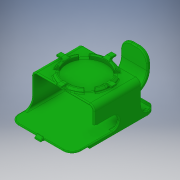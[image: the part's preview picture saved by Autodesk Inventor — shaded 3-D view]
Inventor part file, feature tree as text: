
AUTODESK INVENTOR PART (.ipt)
format: ipt  version: 2019.4 (Build 234330000, 330)  size: 2,206,208 bytes
history: native  units: in
note: dims shown in document units (in); Inventor stores cm internally (conversion verified against a paired STEP export)
features: sketch x43, extrude x41, fillet x30, other x8, reference x8, plane x7, projected_geometry x7, chamfer x5, pattern_circular x1
ambient origin geometry x8: Origin, YZ Plane, XZ Plane, XY Plane, X Axis, Y Axis, Z Axis, Center Point
bodies: Solid1 (feature_tree)
feature tree (150):
  plane  "Work Plane1"
  other  "BasePlate"
  extrude  "Extrusion1"  Depth=0.748in
  extrude  "Extrusion2"  Depth=0.748in
  sketch  "Sketch2"  dims[d0=0.5906in d3=0.748in]
  plane  "Work Plane2"
  extrude  "Extrusion3"  Depth=0.3937in TaperAngle=0.0deg
  extrude  "Extrusion4"  TaperAngle=0.0deg  [1 undecoded]
  extrude  "Extrusion5"  Depth=0.0394in TaperAngle=0.0deg
  extrude  "Extrusion6"  Depth=0.5906in TaperAngle=0.0deg
  plane  "Work Plane4"
  sketch  "Sketch6"  dims[d9=0.2559in d10=0.0in]
  plane  "Work Plane3"
  plane  "Work Plane6"
  extrude  "Extrusion9"  Depth=0.3937in
  fillet  "Fillet13"  Radius=0.5906in
  plane  "Work Plane7"
  extrude  "Extrusion10"  Depth=0.5906in
  sketch  "Sketch13"  dims[d15=3.937in d16=0.5906in d17=0.0in]
  extrude  "Extrusion12"  Depth=0.2362in TaperAngle=0.0deg
  extrude  "Extrusion13"  Depth=0.2362in TaperAngle=0.0deg
  extrude  "Extrusion14"  Depth=0.0787in TaperAngle=0.0deg
  extrude  "Extrusion15"  Depth=0.3543in TaperAngle=0.0deg
  extrude  "Extrusion16"  Depth=0.0394in TaperAngle=0.0deg
  extrude  "Extrusion17"  Depth=0.0787in TaperAngle=0.0deg
  extrude  "Extrusion18"  TaperAngle=0.0deg  [1 undecoded]
  extrude  "Extrusion19"  Depth=0.1969in TaperAngle=0.0deg
  sketch  "Sketch22"  dims[d85=0.1378in d86=0.0in]
  sketch  "Sketch23"  dims[d87=0.8519in d88=0.0in d89=0.1969in d90=0.0in]
  plane  "Work Plane8"
  extrude  "Extrusion20"  Depth=0.1378in
  extrude  "Extrusion21"  Depth=0.0787in
  extrude  "Extrusion22"  Depth=0.1181in TaperAngle=0.0deg
  extrude  "Extrusion23"  Depth=0.0394in
  extrude  "Extrusion24"  Depth=0.1181in TaperAngle=0.0deg
  extrude  "Extrusion25"  Depth=0.0394in
  chamfer  "Chamfer2"  Distance=2.3622in Angle=360.0deg
  extrude  "Extrusion26"  Depth=0.1181in TaperAngle=0.0deg
  chamfer  "Chamfer3"  Distance=0.1102in Angle=45.0deg
  extrude  "Extrusion27"  Depth=0.3937in
  extrude  "Extrusion28"  Depth=0.1181in TaperAngle=45.0deg
  fillet  "Fillet16"  Radius=0.0787in
  chamfer  "Chamfer4"  Distance=0.0787in
  fillet  "Fillet17"  Radius=0.0787in
  fillet  "Fillet18"  Radius=0.0787in
  fillet  "Fillet19"  Radius=0.0394in
  chamfer  "Chamfer5"  Distance=0.0394in
  extrude  "Extrusion29"  Depth=0.7874in
  extrude  "Extrusion30"  Depth=0.0394in TaperAngle=0.0deg
  extrude  "Extrusion31"  Depth=0.0394in TaperAngle=0.0deg
  extrude  "Extrusion32"  Depth=0.1575in
  extrude  "Extrusion33"  Depth=0.1181in TaperAngle=0.0deg
  extrude  "Extrusion34"  Depth=0.1289in TaperAngle=45.0deg
  fillet  "Fillet30"  Radius=0.5413in
  extrude  "Extrusion35"  Depth=1.9685in
  extrude  "Extrusion36"  Depth=2.3622in
  extrude  "Extrusion37"  Depth=0.0394in TaperAngle=0.0deg
  extrude  "Extrusion38"  Depth=0.0394in TaperAngle=0.0deg
  extrude  "Extrusion39"  Depth=0.4828in
  fillet  "Fillet31"  Radius=0.2953in
  chamfer  "Chamfer7"  Distance=0.063in
  fillet  "Fillet32"  Radius=0.063in
  sketch  "Sketch42"  dims[d181=1.9685in d182=2.3622in]
  sketch  "Sketch43"  dims[d183=2.3622in d184=0.0394in d185=0.0in]
  extrude  "Extrusion40"  Depth=0.063in
  sketch  "Sketch45"  dims[d209=0.1181in d210=0.0in d219=0.4828in d220=0.2953in]
  extrude  "Extrusion41"  Depth=0.0394in
  extrude  "Extrusion42"  Depth=0.0394in
  extrude  "Extrusion43"  Depth=0.0394in
  fillet  "Fillet59"  Radius=0.0394in
  fillet  "Fillet60"  Radius=0.0394in
  fillet  "Fillet61"  Radius=0.1019in
  fillet  "Fillet62"  Radius=0.1019in
  fillet  "Fillet63"  Radius=0.1019in
  fillet  "Fillet64"  Radius=0.2165in
  fillet  "Fillet65"  Radius=0.2165in
  fillet  "Fillet66"  Radius=0.2165in
  fillet  "Fillet67"  Radius=0.2165in
  fillet  "Fillet68"  Radius=0.2165in
  fillet  "Fillet69"  Radius=0.2165in
  fillet  "Fillet70"  Radius=0.0394in
  fillet  "Fillet71"  Radius=0.1744in
  fillet  "Fillet72"  Radius=0.0787in
  fillet  "Fillet73"  Radius=1.5748in
  fillet  "Fillet74"  Radius=0.252in
  sketch  "Sketch49"  dims[d224=0.9828in]
  fillet  "Fillet75"  Radius=0.0945in
  extrude  "Extrusion44"  Depth=0.0945in
  pattern_circular  "Circular Pattern1"  [2 undecoded]
  fillet  "Fillet76"  Radius=0.0157in
  fillet  "Fillet77"  Radius=0.0157in
  fillet  "Fillet78"  [1 undecoded]
  fillet  "Fillet79"  [1 undecoded]
  fillet  "Fillet80"  [1 undecoded]
  reference  "Reference1"
  other  "Sideplate1"
  reference  "Reference2"
  reference  "Reference3"
  sketch  "Sketch4"  dims[d4=0.748in d5=0.748in]
  projected_geometry  "Projected Loop1"
  sketch  "Sketch5"  dims[d6=0.748in d7=0.3937in d8=0.0in]
  sketch  "Sketch11"  dims[d11=0.3937in d12=0.0394in d13=0.0in]
  projected_geometry  "Projected Loop4"
  sketch  "Sketch14"  dims[d18=0.5906in d19=0.0in d20=0.3937in d21=0.5906in]
  sketch  "Sketch15"  dims[d22=0.5906in d23=0.0in d33=0.5906in]
  sketch  "Sketch16"  dims[d34=3.937in d36=360.0deg d54=0.2362in d55=0.0in]
  sketch  "Sketch17"  dims[d59=0.25in d60=0.2362in d61=0.0in]
  sketch  "Sketch18"  dims[d69=0.3543in d70=0.0in d71=0.0787in d72=0.0in]
  sketch  "Sketch19"  dims[d73=0.0394in d74=0.0in d75=0.3543in d76=0.0in]
  sketch  "Sketch20"  dims[d77=0.3543in d78=0.0in d79=0.0394in d80=0.0in]
  sketch  "Sketch21"  dims[d81=0.1575in d82=0.0in d83=0.0787in d84=0.0in]
  sketch  "Sketch24"  dims[d91=0.1969in d92=0.0in d93=0.1378in]
  sketch  "Sketch25"  dims[d94=0.0in d95=0.0787in]
  sketch  "Sketch26"  dims[d96=0.0787in d97=0.1181in d98=0.0in]
  sketch  "Sketch27"  dims[d99=0.1181in d100=0.125in d101=45.0deg d102=0.0394in]
  reference  "Reference11"
  reference  "Reference12"
  sketch  "Sketch28"  dims[d103=0.0787in d104=0.1181in d105=0.0in]
  reference  "Reference13"
  sketch  "Sketch29"  dims[d106=0.1181in d107=0.125in d108=45.0deg d109=0.0394in]
  reference  "Reference14"
  sketch  "Sketch30"  dims[d110=0.1181in d111=2.3622in d113=360.0deg]
  sketch  "Sketch31"  dims[d115=0.1181in d116=0.0in d117=0.1181in d118=0.0in]
  sketch  "Sketch32"  dims[d119=0.3543in d120=0.1102in d121=0.125in d122=45.0deg]
  sketch  "Sketch33"  dims[d123=0.3543in d124=0.3937in]
  sketch  "Sketch34"  dims[d125=0.3937in d126=0.1181in d127=0.125in d128=45.0deg d139=0.0787in d140=0.0in d141=0.0787in d142=0.0in d143=0.0787in d144=0.0in d145=0.0787in d146=0.0in d147=0.0394in d148=0.0in d149=0.0394in d150=0.0in]
  sketch  "Sketch35"  dims[d151=0.2913in d155=0.7874in]
  sketch  "Sketch36"  dims[d156=0.0394in d157=0.0in d159=0.0394in d160=0.0in]
  sketch  "Sketch37"  dims[d161=0.0in d162=0.0in d163=0.0394in d164=0.0in]
  projected_geometry  "Projected Loop5"
  sketch  "Sketch38"  dims[d165=0.3937in d166=0.1575in]
  projected_geometry  "Projected Loop6"
  sketch  "Sketch39"  dims[d168=3.7244in d169=0.1181in d170=0.0984in d171=0.0in d172=0.0in]
  sketch  "Sketch40"  dims[d173=0.2913in d174=0.1289in d175=0.125in d176=45.0deg d177=0.5413in]
  sketch  "Sketch41"  dims[d178=0.0394in d180=1.9685in]
  sketch  "Sketch44"  dims[d202=0.0394in d203=0.0in d204=0.0394in d205=0.0in]
  projected_geometry  "Projected Loop7"
  sketch  "Sketch46"  dims[d221=0.1703in]
  sketch  "Sketch47"  dims[d222=0.1078in]
  sketch  "Sketch48"  dims[d223=0.7328in]
  sketch  "Sketch50"  dims[d225=0.6078in d226=0.063in d227=0.063in d228=0.063in d229=0.0394in d230=0.0394in d231=0.0394in d232=0.0394in d233=0.0394in d234=0.1019in d235=0.1019in d236=0.1019in d237=0.2165in d238=0.2165in d239=0.2165in d240=0.2165in d241=0.2165in d242=0.2165in d243=0.2165in d244=0.2165in d245=0.0394in d246=0.1744in d247=0.0787in d248=0.0in d249=1.5748in d250=360.0deg d252=0.252in d253=0.0945in d254=0.0945in d255=1.6654in d256=0.0157in d257=0.0157in]
  reference  "Reference15"
  other  "<userpath>\OneDrive - Eastside Preparatory School\Documents\Inventor\GPSUnitCase.iam"
  other  "GPSUnitCase.iam"
  other  "GPSUnitAssembly:1"
  other  "OrionUnit"
  other  "Puck:1"
  projected_geometry  "Project Cut Edges1"
  projected_geometry  "Project Cut Edges2"
  other  "<userpath>\Documents\Inventor\GPSUnitCase.iam"
note: 7 required parameter values undecoded (feature->parameter linkage not recoverable at this tier; creation-order binding heuristic only, values carry confidence <= 0.55)
